FCSTD DOCUMENT  (FreeCAD 0.19R24276 (Git))
Label: Z-belt_for_bldc_z_axis
License: All rights reserved
LicenseURL: http://en.wikipedia.org/wiki/All_rights_reserved
objects: Sketcher::SketchObject×1, PartDesign::Body×1
note: 2 computed .brp shape members not serialized (recipe doc carries the construction recipe); baked Part::Feature solids carry a one-line shape summary decoded from their .brp

FEATURE [Sketcher::SketchObject] Sketch
  FullyConstrained = false
  MapMode = 5
  Support = -> [XY_Plane]
  sketch-geometry (16):
    g0: Circle CenterX=0 CenterY=0 CenterZ=0 NormalX=0 NormalY=0 NormalZ=1 AngleXU=0 Radius=28.5
    g1: Circle CenterX=277.928 CenterY=0 CenterZ=0 NormalX=0 NormalY=0 NormalZ=1 AngleXU=0 Radius=62.5
    g2: LineSegment StartX=35 StartY=65 StartZ=0 EndX=35 EndY=-65 EndZ=0
    g3: LineSegment StartX=35 StartY=25 StartZ=0 EndX=35 EndY=65 EndZ=0
    g4: LineSegment StartX=0 StartY=0 StartZ=0 EndX=35 EndY=0 EndZ=0
    g5: LineSegment StartX=35 StartY=-25 StartZ=0 EndX=35 EndY=-65 EndZ=0
    g6: Circle CenterX=277.928 CenterY=0 CenterZ=0 NormalX=0 NormalY=0 NormalZ=1 AngleXU=0 Radius=70
    g7: LineSegment StartX=-3.48647 StartY=28.2859 StartZ=0 EndX=270.282 EndY=62.0306 EndZ=0
    g8: LineSegment StartX=-3.48651 StartY=-28.2859 StartZ=0 EndX=270.282 EndY=-62.0306 EndZ=0
    g9: LineSegment StartX=0 StartY=0 StartZ=0 EndX=-3.48651 EndY=-28.2859 EndZ=0
    g10: LineSegment StartX=0 StartY=0 StartZ=0 EndX=-3.48647 EndY=28.2859 EndZ=0
    g11: LineSegment StartX=277.928 StartY=0 StartZ=0 EndX=270.282 EndY=62.0306 EndZ=0
    g12: LineSegment StartX=277.928 StartY=0 StartZ=0 EndX=270.282 EndY=-62.0306 EndZ=0
    g13: LineSegment StartX=277.928 StartY=0 StartZ=0 EndX=277.928 EndY=-62.5 EndZ=0
    g14: LineSegment StartX=0 StartY=0 StartZ=0 EndX=0 EndY=28.5 EndZ=0
    g15: LineSegment StartX=277.928 StartY=0 StartZ=0 EndX=277.928 EndY=62.5 EndZ=0
  constraints (42):
    c: Coincident(g0,g-1)
    c: PointOnObject(g1,g-1)
    c: Diameter(g0) = 57
    c: Diameter(g1) = 125
    c: Vertical(g2)
    c: DistanceX(g0,g2) = 35
    c: Vertical(g3)
    c: Coincident(g4,g0)
    c: PointOnObject(g4,g-1)
    c: Symmetric(g2,g2,g4)
    c: Parallel(g5,g2)
    c: DistanceY(g2,g2) = 130
    c: Coincident(g6,g1)
    c: Diameter(g6) = 140
    c: DistanceY(g3,g2) = 40
    c: DistanceY(g2,g5) = 40
    c: PointOnObject(g7,g0)
    c: PointOnObject(g7,g1)
    c: Tangent(g7,g0)
    c: PointOnObject(g8,g0)
    c: PointOnObject(g8,g1)
    c: Tangent(g8,g1)
    c: Coincident(g9,g0)
    c: Coincident(g11,g1)
    c: Coincident(g11,g7)
    c: Perpendicular(g11,g7)
    c: Coincident(g12,g1)
    c: Coincident(g12,g8)
    c: Coincident(g8,g9)
    c: Perpendicular(g8,g9)
    c: Coincident(g10,g0)
    c: Coincident(g10,g7)
    c: Coincident(g13,g1)
    c: Vertical(g13)
    c: PointOnObject(g13,g1)
    c: Coincident(g14,g0)
    c: PointOnObject(g14,g0)
    c: Coincident(g15,g1)
    c: Vertical(g15)
    c: PointOnObject(g15,g1)
    c: Distance(g14,g15) = 280
    c: Vertical(g14)
FEATURE [PartDesign::Body] Body
  Group = -> [Sketch]
  Origin = -> Origin
